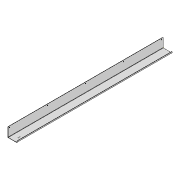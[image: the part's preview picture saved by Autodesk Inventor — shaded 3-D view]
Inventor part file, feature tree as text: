
AUTODESK INVENTOR PART (.ipt)
format: ipt  version: 2020 (Build 240168000, 168)  size: 149,504 bytes
history: native  units: mm
features: other x10, sketch x6, hole x2, fillet x1
ambient origin geometry x8: Origin, YZ Plane, XZ Plane, XY Plane, X Axis, Y Axis, Z Axis, Center Point
bodies: Body1 (feature_tree)
feature tree (19):
  other  "ソリッド1"
  other  "フランジ1"
  other  "フランジ2"
  fillet  "フィレット1"  Radius=60.0mm
  sketch  "スケッチ4"
  hole  "穴1"  [1 undecoded]
  hole  "穴2"  [1 undecoded]
  sketch  "スケッチ1"
  other  "プレート1"
  sketch  "スケッチ2"
  other  "プレート2"
  other  "曲げ1"
  other  "コーナー1"
  sketch  "スケッチ3"
  other  "プレート3"
  other  "曲げ2"
  other  "コーナー2"
  sketch  "スケッチ5"
  sketch  "スケッチ6"
note: 2 required parameter values undecoded (feature->parameter linkage not recoverable at this tier; creation-order binding heuristic only, values carry confidence <= 0.55)
